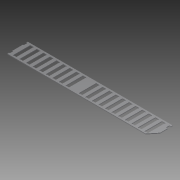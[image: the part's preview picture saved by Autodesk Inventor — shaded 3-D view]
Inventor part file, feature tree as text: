
AUTODESK INVENTOR PART (.ipt)
format: ipt  version: 2013 (Build 170138000, 138)  size: 243,200 bytes
history: native  units: in
note: dims shown in document units (in); Inventor stores cm internally (conversion verified against a paired STEP export)
features: extrude x5, sketch x5, projected_geometry x2
ambient origin geometry x8: Origin, YZ Plane, XZ Plane, XY Plane, X Axis, Y Axis, Z Axis, Center Point
bodies: Solid1 (feature_tree)
feature tree (12):
  extrude  "Extrusion1"  Depth=22.0in
  extrude  "Extrusion2"  Depth=0.5in
  extrude  "Extrusion3"  Depth=0.5in
  extrude  "Extrusion4"  Depth=0.125in TaperAngle=0.0deg
  extrude  "Extrusion5"  Depth=0.5in
  sketch  "Sketch1"  dims[d0=3.125in d1=22.0in]
  sketch  "Sketch3"  dims[d2=0.125in d3=0.0in d4=0.5in]
  sketch  "Sketch4"  dims[d5=0.25in d6=0.5in]
  projected_geometry  "Projected Loop1"
  projected_geometry  "Projected Loop2"
  sketch  "Sketch5"  dims[d7=0.25in d8=0.125in d9=0.0in]
  sketch  "Sketch6"  dims[d10=0.25in d11=0.0in d12=0.5in d14=0.625in d15=0.25in d16=0.25in d17=8.2677in d19=1.0in d20=0.3937in d22=1.0in d24=1.0in d25=0.0in d26=0.3436in d27=1.0in d28=1.0in d29=0.0in]
